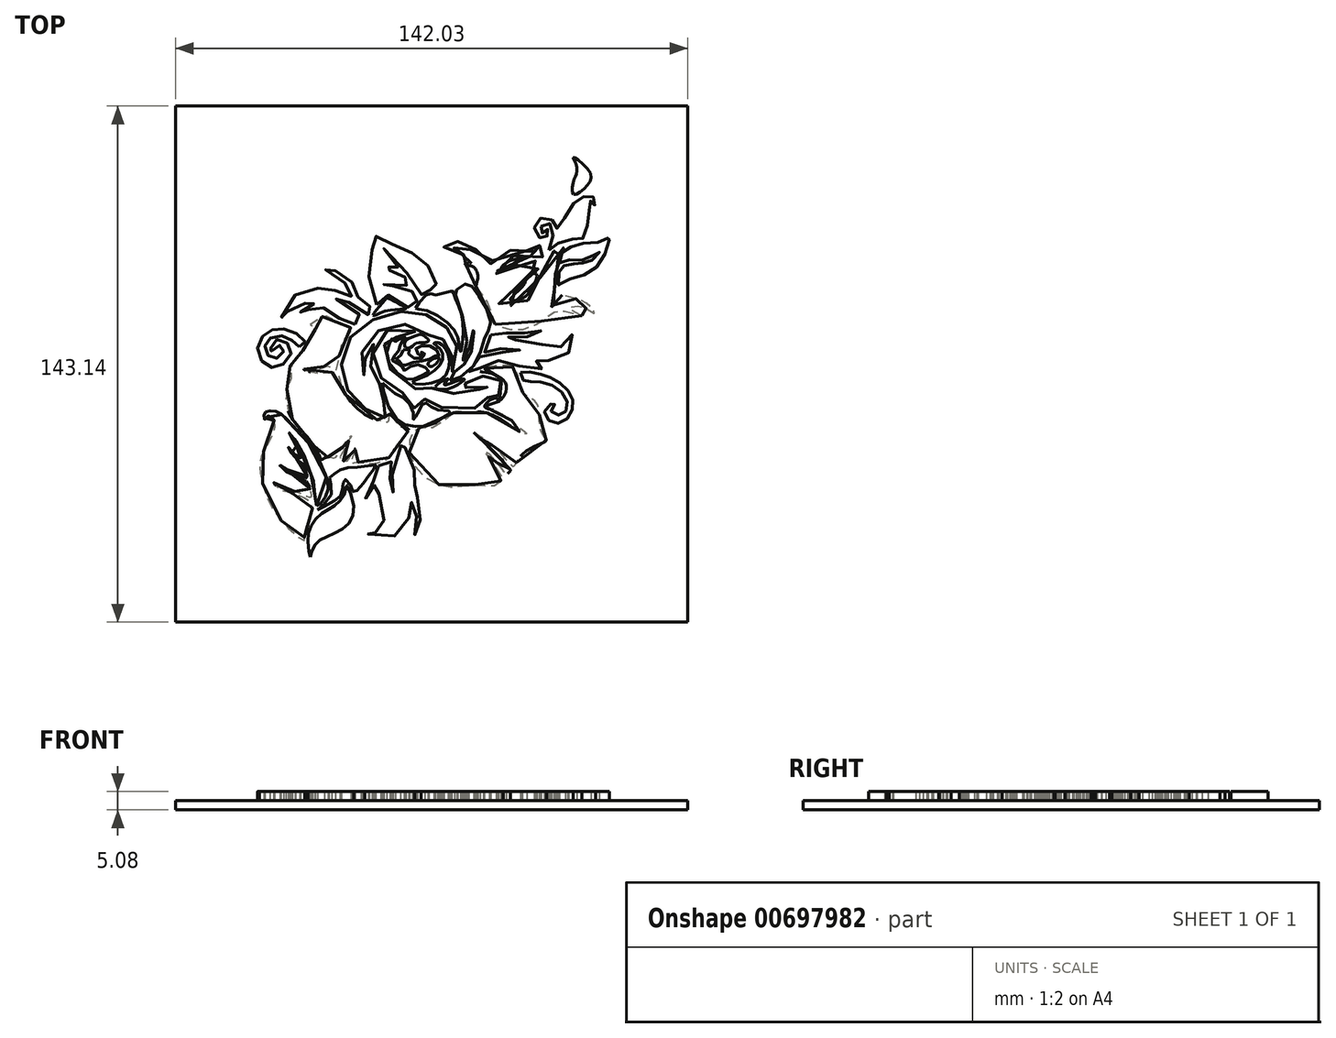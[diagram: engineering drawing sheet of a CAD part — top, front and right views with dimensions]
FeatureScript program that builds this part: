
annotation { "Feature Type Name" : "Feature", "Feature Type Description" : "" }
export const myFeature = defineFeature(function(context is Context, id is Id, definition is map)
    precondition{}
    {
        {
            var Q0;
            Q0=qCreatedBy(makeId("Top.planeOp"),FACE);
            var sketch = newSketch(context, id + "F0", { "sketchPlane" : qUnion([Q0])});
            skLineSegment(sketch, "E0.bottom", {"start": v(-70.24, 72.03) * mm, "end": v(71.8, 72.03) * mm});
            skLineSegment(sketch, "E0.top", {"start": v(-70.24, -71.11) * mm, "end": v(71.8, -71.11) * mm});
            skLineSegment(sketch, "E0.left", {"start": v(-70.24, 72.03) * mm, "end": v(-70.24, -71.11) * mm});
            skLineSegment(sketch, "E0.right", {"start": v(71.8, 72.03) * mm, "end": v(71.8, -71.11) * mm});
            skSolve(sketch);
        }
        {
            var Q0;
            Q0=qCreatedBy(makeId("Top.planeOp"),FACE);
            cPlane(context, id + "F1", {"entities" : qUnion([Q0]), "cplaneType" : CPlaneType.OFFSET, "offset" : 2.54 * mm, "width" : 152.4 * mm, "height" : 152.4 * mm});
        }
        {
            var Q0;
            Q0=makeQuery(id+"F0.imprint","IMPRINT",FACE,{"disambiguationData":[TD([[makeQuery(id+"F0.imprint","IMPRINT",EDGE,{"derivedFrom":sQuery(id+"F0.wireOp",EDGE,"E0.bottom")}),-1.0]])]});
            extrude(context, id + "F2", {"entities" : qUnion([Q0]), "depth" : 2.54 * mm, "offsetDistance" : 25.4 * mm});
        }
        {
            var Q0;
            Q0=makeQuery(id+"F2.opExtrude","CAP_FACE",FACE,{"disambiguationData":[OSD([sQuery(id+"F0.wireOp",EDGE,"E0.bottom"),sQuery(id+"F0.wireOp",EDGE,"E0.top"),sQuery(id+"F0.wireOp",EDGE,"E0.left"),sQuery(id+"F0.wireOp",EDGE,"E0.right")])],"isStart":false});
            var sketch = newSketch(context, id + "F3", { "sketchPlane" : qUnion([Q0])});
            skFitSpline(sketch, "E1", {"points": [v(-35.94, 5.21) * mm, v(-34.32, 6.4) * mm, v(-37.33, 9.33) * mm, v(-42.18, 10.2) * mm, v(-45.56, 8.7) * mm, v(-47.5, 4.27) * mm, v(-44.77, 0) * mm, v(-41.11, 0) * mm, v(-38.06, 3.91) * mm, v(-40.5, 7.1) * mm, v(-43.21, 6.5) * mm, v(-43.93, 3.58) * mm, v(-42.6, 5.3) * mm, v(-40.5, 5.3) * mm, v(-40.68, 3.08) * mm, v(-43.35, 2.02) * mm, v(-45.25, 4.12) * mm, v(-44.95, 6.79) * mm, v(-41.8, 8.33) * mm, v(-38.2, 7.27) * mm, v(-35.94, 5.21) * mm]});
            skSolve(sketch);
        }
        {
            var Q0;
            Q0=makeQuery(id+"F3.imprint","IMPRINT",FACE,{"disambiguationData":[TD([[makeQuery(id+"F3.imprint","IMPRINT",EDGE,{"derivedFrom":sQuery(id+"F3.wireOp",EDGE,"E1")}),1.0]])]});
            extrude(context, id + "F4", {"entities" : qUnion([Q0]), "operationType" : NewBodyOperationType.ADD, "depth" : 2.54 * mm, "offsetDistance" : 25.4 * mm});
        }
        {
            var Q0;
            Q0=qCreatedBy(id+"F1.planeOp",FACE);
            var sketch = newSketch(context, id + "F5", { "sketchPlane" : qUnion([Q0])});
            skFitSpline(sketch, "E2", {"points": [v(-20.47, 11.53) * mm, v(-18.42, 13.18) * mm, v(-25.91, 18.74) * mm, v(-20.95, 17.01) * mm, v(-16.07, 14.1) * mm, v(-16.07, 16.11) * mm, v(-19.16, 18.41) * mm, v(-20.72, 21.86) * mm, v(-24.08, 25.62) * mm, v(-28.9, 26.88) * mm, v(-24.94, 24.5) * mm, v(-21.15, 19.34) * mm, v(-24.94, 20.58) * mm, v(-28.94, 21.4) * mm, v(-37.09, 19.6) * mm, v(-40.97, 12.78) * mm, v(-38.37, 15.97) * mm, v(-33.01, 17.43) * mm, v(-31.62, 17.34) * mm, v(-33.87, 16.32) * mm, v(-35.83, 14.35) * mm, v(-33.16, 15.68) * mm, v(-29.38, 16.15) * mm, v(-24.5, 13.03) * mm, v(-20.47, 11.53) * mm]});
            skSolve(sketch);
        }
        {
            var Q0;
            Q0=makeQuery(id+"F5.imprint","IMPRINT",FACE,{"disambiguationData":[TD([[makeQuery(id+"F5.imprint","IMPRINT",EDGE,{"derivedFrom":sQuery(id+"F5.wireOp",EDGE,"E2")}),1.0]])]});
            extrude(context, id + "F6", {"entities" : qUnion([Q0]), "operationType" : NewBodyOperationType.ADD, "depth" : 2.54 * mm, "offsetDistance" : 25.4 * mm});
        }
        {
            var Q0;
            Q0=qCreatedBy(id+"F1.planeOp",FACE);
            var sketch = newSketch(context, id + "F7", { "sketchPlane" : qUnion([Q0])});
            skFitSpline(sketch, "E3", {"points": [v(-14.47, 17) * mm, v(-12.08, 19.37) * mm, v(-10.76, 19.34) * mm, v(-5.19, 16.12) * mm, v(-4.45, 17.02) * mm, v(-3.25, 18.12) * mm, v(-3.7, 19.39) * mm, v(-4.65, 20.6) * mm, v(-8.74, 22.16) * mm, v(-13.33, 22.03) * mm, v(-10.14, 23) * mm, v(-5.64, 22.3) * mm, v(-6.08, 23.41) * mm, v(-6.89, 24.97) * mm, v(-10.14, 26.28) * mm, v(-12.86, 27.16) * mm, v(-9.57, 27.16) * mm, v(-7.86, 26.51) * mm, v(-12.56, 32.43) * mm, v(-5.4, 24.8) * mm, v(-1.93, 19.73) * mm, v(-1.33, 20.28) * mm, v(0, 21.03) * mm, v(2.38, 20.98) * mm, v(1.83, 23.22) * mm, v(0, 27.49) * mm, v(-3.68, 30.7) * mm, v(-8.37, 33.18) * mm, v(-13.3, 34.82) * mm, v(-14.89, 35.97) * mm, v(-15.46, 33.45) * mm, v(-16.66, 27.43) * mm, v(-14.47, 17) * mm]});
            skSolve(sketch);
        }
        {
            var Q0;
            Q0=makeQuery(id+"F7.imprint","IMPRINT",FACE,{"disambiguationData":[TD([[makeQuery(id+"F7.imprint","IMPRINT",EDGE,{"derivedFrom":sQuery(id+"F7.wireOp",EDGE,"E3")}),1.0]])]});
            extrude(context, id + "F8", {"entities" : qUnion([Q0]), "operationType" : NewBodyOperationType.ADD, "depth" : 2.54 * mm, "offsetDistance" : 25.4 * mm});
        }
        {
            var Q0;
            Q0=makeQuery(id+"F2.opExtrude","CAP_FACE",FACE,{"disambiguationData":[OSD([sQuery(id+"F0.wireOp",EDGE,"E0.bottom"),sQuery(id+"F0.wireOp",EDGE,"E0.top"),sQuery(id+"F0.wireOp",EDGE,"E0.left"),sQuery(id+"F0.wireOp",EDGE,"E0.right")])],"isStart":false});
            var sketch = newSketch(context, id + "F9", { "sketchPlane" : qUnion([Q0])});
            skFitSpline(sketch, "E4", {"points": [v(13.15, 21.94) * mm, v(15.72, 18.44) * mm, v(18.2, 11.98) * mm, v(18.88, 11.18) * mm, v(25.15, 9.95) * mm, v(32.75, 13.51) * mm, v(36.96, 15.31) * mm, v(42.41, 13.88) * mm, v(38.74, 16.03) * mm, v(39.71, 16.4) * mm, v(42.83, 16.35) * mm, v(46.16, 14.51) * mm, v(44.79, 16.6) * mm, v(40.46, 18.72) * mm, v(37.5, 19.43) * mm, v(36.17, 19.7) * mm, v(35.7, 18.87) * mm, v(34.14, 16.35) * mm, v(35.04, 19.33) * mm, v(35.23, 23.76) * mm, v(35.1, 28.34) * mm, v(36.32, 31.34) * mm, v(37.92, 32.7) * mm, v(35.31, 32.12) * mm, v(32.43, 29.72) * mm, v(30.8, 24.09) * mm, v(29.12, 19.93) * mm, v(24.94, 16.98) * mm, v(19.36, 17.1) * mm, v(22.43, 18.85) * mm, v(23.84, 20.87) * mm, v(25.71, 24.06) * mm, v(28.11, 26.11) * mm, v(30.06, 26.68) * mm, v(30.67, 28.18) * mm, v(30, 28.97) * mm, v(27.54, 28.88) * mm, v(23.97, 27.6) * mm, v(21.73, 25.87) * mm, v(18.97, 24.78) * mm, v(18.78, 25.76) * mm, v(20.83, 28.62) * mm, v(24.2, 30.72) * mm, v(29.3, 30.25) * mm, v(32.4, 30.54) * mm, v(32.52, 32.34) * mm, v(31.51, 33.12) * mm, v(30.03, 33.4) * mm, v(30.87, 32.6) * mm, v(30.73, 31.78) * mm, v(28.6, 31.86) * mm, v(26.46, 31.95) * mm, v(21.55, 31.93) * mm, v(18.32, 30.33) * mm, v(17.07, 28.15) * mm, v(16.18, 30.41) * mm, v(13.01, 32.26) * mm, v(10.22, 32.48) * mm, v(8.03, 34.52) * mm, v(8.73, 32.75) * mm, v(6.1, 32.81) * mm, v(3.49, 32.71) * mm, v(7.3, 31.55) * mm, v(10.78, 30.04) * mm, v(12.8, 28.15) * mm, v(11.49, 28.43) * mm, v(10.02, 28.21) * mm, v(11.34, 27.77) * mm, v(12.84, 27) * mm, v(13.58, 24.09) * mm, v(13.15, 21.94) * mm]});
            skSolve(sketch);
        }
        {
            var Q0;
            Q0=makeQuery(id+"F9.imprint","IMPRINT",FACE,{"disambiguationData":[TD([[makeQuery(id+"F9.imprint","IMPRINT",EDGE,{"derivedFrom":sQuery(id+"F9.wireOp",EDGE,"E4")}),1.0]])]});
            extrude(context, id + "F10", {"entities" : qUnion([Q0]), "operationType" : NewBodyOperationType.ADD, "depth" : 2.54 * mm, "offsetDistance" : 25.4 * mm});
        }
        {
            var Q0;
            Q0=qCreatedBy(id+"F1.planeOp",FACE);
            var sketch = newSketch(context, id + "F11", { "sketchPlane" : qUnion([Q0])});
            skFitSpline(sketch, "E5", {"points": [v(25.88, 29.7) * mm, v(21.93, 28.86) * mm, v(20.05, 26.64) * mm, v(22.53, 27.37) * mm, v(23.88, 28.63) * mm, v(25.88, 29.7) * mm]});
            skSolve(sketch);
        }
        {
            var Q0;
            Q0=makeQuery(id+"F11.imprint","IMPRINT",FACE,{"disambiguationData":[TD([[makeQuery(id+"F11.imprint","IMPRINT",EDGE,{"derivedFrom":sQuery(id+"F11.wireOp",EDGE,"E5")}),1.0]])]});
            extrude(context, id + "F12", {"entities" : qUnion([Q0]), "operationType" : NewBodyOperationType.ADD, "depth" : 2.54 * mm, "offsetDistance" : 25.4 * mm});
        }
        {
            var Q0;
            Q0=qCreatedBy(id+"F1.planeOp",FACE);
            var sketch = newSketch(context, id + "F13", { "sketchPlane" : qUnion([Q0])});
            skFitSpline(sketch, "E6", {"points": [v(29.83, 25.45) * mm, v(27.47, 24.85) * mm, v(26.24, 22.34) * mm, v(22.55, 18.26) * mm, v(25.89, 18.76) * mm, v(28.44, 21.31) * mm, v(29.83, 25.45) * mm]});
            skSolve(sketch);
        }
        {
            var Q0;
            Q0=makeQuery(id+"F13.imprint","IMPRINT",FACE,{"disambiguationData":[TD([[makeQuery(id+"F13.imprint","IMPRINT",EDGE,{"derivedFrom":sQuery(id+"F13.wireOp",EDGE,"E6")}),1.0]])]});
            extrude(context, id + "F14", {"entities" : qUnion([Q0]), "operationType" : NewBodyOperationType.ADD, "depth" : 2.54 * mm, "offsetDistance" : 25.4 * mm});
        }
        {
            var Q0;
            Q0=qCreatedBy(id+"F1.planeOp",FACE);
            var sketch = newSketch(context, id + "F15", { "sketchPlane" : qUnion([Q0])});
            skFitSpline(sketch, "E7", {"points": [v(33.28, 32.03) * mm, v(36.18, 34.2) * mm, v(41.06, 35.12) * mm, v(43, 35.65) * mm, v(44.2, 41.55) * mm, v(44.64, 44.66) * mm, v(44.94, 45.8) * mm, v(45.94, 44.52) * mm, v(46.08, 46) * mm, v(44.92, 47.11) * mm, v(42, 46.57) * mm, v(38.63, 42.9) * mm, v(35.62, 38.12) * mm, v(34.77, 39.73) * mm, v(31.8, 41.15) * mm, v(29.4, 39.14) * mm, v(30.28, 35.73) * mm, v(32.24, 35.6) * mm, v(33.04, 36.43) * mm, v(33.01, 37.9) * mm, v(32.38, 36.75) * mm, v(31.07, 37.21) * mm, v(31.04, 38.52) * mm, v(32.65, 39.53) * mm, v(34.64, 38.1) * mm, v(33.28, 32.03) * mm]});
            skSolve(sketch);
        }
        {
            var Q0;
            Q0=makeQuery(id+"F15.imprint","IMPRINT",FACE,{"disambiguationData":[TD([[makeQuery(id+"F15.imprint","IMPRINT",EDGE,{"derivedFrom":sQuery(id+"F15.wireOp",EDGE,"E7")}),1.0]])]});
            extrude(context, id + "F16", {"entities" : qUnion([Q0]), "operationType" : NewBodyOperationType.ADD, "depth" : 2.54 * mm, "offsetDistance" : 25.4 * mm});
        }
        {
            var Q0;
            Q0=qCreatedBy(id+"F1.planeOp",FACE);
            var sketch = newSketch(context, id + "F17", { "sketchPlane" : qUnion([Q0])});
            skFitSpline(sketch, "E8", {"points": [v(40.15, 47.54) * mm, v(43.66, 49.75) * mm, v(44.73, 53.5) * mm, v(40.13, 57.8) * mm, v(40.75, 56.07) * mm, v(40.89, 53.24) * mm, v(40.07, 51.06) * mm, v(40.15, 47.54) * mm]});
            skSolve(sketch);
        }
        {
            var Q0;
            Q0=makeQuery(id+"F17.imprint","IMPRINT",FACE,{"disambiguationData":[TD([[makeQuery(id+"F17.imprint","IMPRINT",EDGE,{"derivedFrom":sQuery(id+"F17.wireOp",EDGE,"E8")}),1.0]])]});
            extrude(context, id + "F18", {"entities" : qUnion([Q0]), "operationType" : NewBodyOperationType.ADD, "depth" : 2.54 * mm, "offsetDistance" : 25.4 * mm});
        }
        {
            var Q0;
            Q0=qCreatedBy(id+"F1.planeOp",FACE);
            var sketch = newSketch(context, id + "F19", { "sketchPlane" : qUnion([Q0])});
            skFitSpline(sketch, "E9", {"points": [v(-15.47, 14) * mm, v(-11.85, 15.19) * mm, v(-6.34, 15.83) * mm, v(-6.92, 16.4) * mm, v(-11.38, 18.72) * mm, v(-12.14, 18.28) * mm, v(-15.47, 14) * mm]});
            skSolve(sketch);
        }
        {
            var Q0;
            Q0=makeQuery(id+"F19.imprint","IMPRINT",FACE,{"disambiguationData":[TD([[makeQuery(id+"F19.imprint","IMPRINT",EDGE,{"derivedFrom":sQuery(id+"F19.wireOp",EDGE,"E9")}),1.0]])]});
            extrude(context, id + "F20", {"entities" : qUnion([Q0]), "operationType" : NewBodyOperationType.ADD, "depth" : 2.54 * mm, "offsetDistance" : 25.4 * mm});
        }
        {
            var Q0;
            Q0=qCreatedBy(id+"F1.planeOp",FACE);
            var sketch = newSketch(context, id + "F21", { "sketchPlane" : qUnion([Q0])});
            skFitSpline(sketch, "E10", {"points": [v(36.07, 25.96) * mm, v(36.12, 21.99) * mm, v(36.65, 22.74) * mm, v(38.91, 23.98) * mm, v(45.13, 26.25) * mm, v(49.24, 31.97) * mm, v(50.03, 35.93) * mm, v(48.92, 34.73) * mm, v(43.4, 34.08) * mm, v(38.54, 32.55) * mm, v(36.44, 30.35) * mm, v(36.23, 27.82) * mm, v(36.7, 28.9) * mm, v(39.94, 29.31) * mm, v(44.63, 29.98) * mm, v(47.32, 31.62) * mm, v(45.68, 29.67) * mm, v(42.9, 28.51) * mm, v(40.3, 28.21) * mm, v(37.42, 27.7) * mm, v(36.07, 25.96) * mm]});
            skSolve(sketch);
        }
        {
            var Q0;
            Q0=makeQuery(id+"F21.imprint","IMPRINT",FACE,{"disambiguationData":[TD([[makeQuery(id+"F21.imprint","IMPRINT",EDGE,{"derivedFrom":sQuery(id+"F21.wireOp",EDGE,"E10")}),1.0]])]});
            extrude(context, id + "F22", {"entities" : qUnion([Q0]), "operationType" : NewBodyOperationType.ADD, "depth" : 2.54 * mm, "offsetDistance" : 25.4 * mm});
        }
        {
            var Q0;
            Q0=qCreatedBy(id+"F1.planeOp",FACE);
            var sketch = newSketch(context, id + "F23", { "sketchPlane" : qUnion([Q0])});
            skFitSpline(sketch, "E11", {"points": [v(17.17, 8.62) * mm, v(15.13, 3.81) * mm, v(16.84, 4.6) * mm, v(20.13, 4.8) * mm, v(25.36, 4.35) * mm, v(24.04, 4.3) * mm, v(20.8, 3.76) * mm, v(14.46, 2.88) * mm, v(12.75, 0) * mm, v(11.08, -1.82) * mm, v(12.97, -1.17) * mm, v(15.43, 0) * mm, v(19.7, 1.43) * mm, v(24.44, 0) * mm, v(28.48, 0) * mm, v(32.61, -1.22) * mm, v(29.46, 1.73) * mm, v(30.3, 1.7) * mm, v(34.96, 1.65) * mm, v(39.18, 4.33) * mm, v(39.78, 8.73) * mm, v(39.35, 7.34) * mm, v(36.37, 5.2) * mm, v(32.49, 5.54) * mm, v(27.45, 6.85) * mm, v(20.84, 7.57) * mm, v(21.94, 7.92) * mm, v(25.88, 8.24) * mm, v(29.02, 8.22) * mm, v(31.15, 9.61) * mm, v(29.02, 9.42) * mm, v(26.07, 9.1) * mm, v(22.75, 9.05) * mm, v(18.76, 9.05) * mm, v(17.17, 8.62) * mm]});
            skSolve(sketch);
        }
        {
            var Q0;
            Q0=makeQuery(id+"F23.imprint","IMPRINT",FACE,{"disambiguationData":[TD([[makeQuery(id+"F23.imprint","IMPRINT",EDGE,{"derivedFrom":sQuery(id+"F23.wireOp",EDGE,"E11")}),1.0]])]});
            extrude(context, id + "F24", {"entities" : qUnion([Q0]), "operationType" : NewBodyOperationType.ADD, "depth" : 2.54 * mm, "offsetDistance" : 25.4 * mm});
        }
        {
            var Q0;
            Q0=qCreatedBy(id+"F1.planeOp",FACE);
            var sketch = newSketch(context, id + "F25", { "sketchPlane" : qUnion([Q0])});
            skFitSpline(sketch, "E12", {"points": [v(25.47, -1.8) * mm, v(26.26, -4.03) * mm, v(28.3, -4.37) * mm, v(32, -4.63) * mm, v(36.46, -6.94) * mm, v(38.43, -10.48) * mm, v(37.32, -13.33) * mm, v(34.83, -13.38) * mm, v(33.8, -11.87) * mm, v(35.09, -10.33) * mm, v(32.57, -11.4) * mm, v(32.64, -14.4) * mm, v(35.35, -15.97) * mm, v(38.63, -14.46) * mm, v(40, -11.06) * mm, v(39.21, -7.68) * mm, v(36.15, -4.65) * mm, v(32.4, -2.73) * mm, v(28.62, -1.82) * mm, v(25.47, -1.8) * mm]});
            skSolve(sketch);
        }
        {
            var Q0;
            Q0=makeQuery(id+"F25.imprint","IMPRINT",FACE,{"disambiguationData":[TD([[makeQuery(id+"F25.imprint","IMPRINT",EDGE,{"derivedFrom":sQuery(id+"F25.wireOp",EDGE,"E12")}),1.0]])]});
            extrude(context, id + "F26", {"entities" : qUnion([Q0]), "operationType" : NewBodyOperationType.ADD, "depth" : 2.54 * mm, "offsetDistance" : 25.4 * mm});
        }
        {
            var Q0;
            Q0=qCreatedBy(id+"F1.planeOp",FACE);
            var sketch = newSketch(context, id + "F27", { "sketchPlane" : qUnion([Q0])});
            skFitSpline(sketch, "E13", {"points": [v(-3.64, 15.96) * mm, v(0, 20.04) * mm, v(1.3, 19.65) * mm, v(6.69, 20.7) * mm, v(6.92, 20.1) * mm, v(8.34, 16.33) * mm, v(9.6, 9.7) * mm, v(8.8, 3.74) * mm, v(8.44, 5.88) * mm, v(6.45, 10.7) * mm, v(-2.04, 15.72) * mm, v(-3.64, 15.96) * mm]});
            skSolve(sketch);
        }
        {
            var Q0;
            Q0=qCreatedBy(id+"F1.planeOp",FACE);
            var sketch = newSketch(context, id + "F28", { "sketchPlane" : qUnion([Q0])});
            skFitSpline(sketch, "E14", {"points": [v(5.88, -4.12) * mm, v(7.69, -1.1) * mm, v(11.35, 2.5) * mm, v(12.45, 10.44) * mm, v(11.21, 4.8) * mm, v(9.13, 1.08) * mm, v(10.55, 7.14) * mm, v(7.15, 21.03) * mm, v(8.03, 21.18) * mm, v(10.7, 22.93) * mm, v(12.56, 21.18) * mm, v(15.5, 16.78) * mm, v(17.15, 10.85) * mm, v(16.25, 9.4) * mm, v(14.7, 4.88) * mm, v(10.88, -1.59) * mm, v(5.88, -4.12) * mm]});
            skSolve(sketch);
        }
        {
            var Q0;
            Q0=makeQuery(id+"F27.imprint","IMPRINT",FACE,{"disambiguationData":[TD([[makeQuery(id+"F27.imprint","IMPRINT",EDGE,{"derivedFrom":sQuery(id+"F27.wireOp",EDGE,"E13")}),-1.0]])]});
            extrude(context, id + "F29", {"entities" : qUnion([Q0]), "operationType" : NewBodyOperationType.ADD, "depth" : 2.54 * mm, "offsetDistance" : 25.4 * mm});
        }
        {
            var Q0;
            Q0=makeQuery(id+"F28.imprint","IMPRINT",FACE,{"disambiguationData":[TD([[makeQuery(id+"F28.imprint","IMPRINT",EDGE,{"derivedFrom":sQuery(id+"F28.wireOp",EDGE,"E14")}),-1.0]])]});
            extrude(context, id + "F30", {"entities" : qUnion([Q0]), "operationType" : NewBodyOperationType.ADD, "depth" : 2.54 * mm, "offsetDistance" : 25.4 * mm});
        }
        {
            var Q0;
            Q0=qCreatedBy(id+"F1.planeOp",FACE);
            var sketch = newSketch(context, id + "F31", { "sketchPlane" : qUnion([Q0])});
            skFitSpline(sketch, "E15", {"points": [v(-12.1, -14.35) * mm, v(-11.75, -11.88) * mm, v(-13.11, -8.32) * mm, v(-13.68, -4.99) * mm, v(-14.9, -2.72) * mm, v(-16.4, 2.64) * mm, v(-15.3, 6.32) * mm, v(-17.2, 3.76) * mm, v(-17.75, -3.13) * mm, v(-18.57, 0) * mm, v(-17.88, 5.28) * mm, v(-11.6, 11.04) * mm, v(-4.3, 10.9) * mm, v(1.08, 8.07) * mm, v(3.3, 7.54) * mm, v(4.35, 6.94) * mm, v(6.23, 3.55) * mm, v(6.32, -2.14) * mm, v(7.41, 2.7) * mm, v(7.34, 7.36) * mm, v(3.5, 11.95) * mm, v(-1.75, 14.52) * mm, v(-8.66, 14.94) * mm, v(-17.07, 11.92) * mm, v(-22.84, 6.19) * mm, v(-24.14, -2.42) * mm, v(-21.31, -8.49) * mm, v(-15.9, -13.13) * mm, v(-12.1, -14.35) * mm]});
            skSolve(sketch);
        }
        {
            var Q0;
            Q0=makeQuery(id+"F31.imprint","IMPRINT",FACE,{"disambiguationData":[TD([[makeQuery(id+"F31.imprint","IMPRINT",EDGE,{"derivedFrom":sQuery(id+"F31.wireOp",EDGE,"E15")}),1.0]])]});
            extrude(context, id + "F32", {"entities" : qUnion([Q0]), "operationType" : NewBodyOperationType.ADD, "depth" : 2.54 * mm, "offsetDistance" : 25.4 * mm});
        }
        {
            var Q0;
            Q0=qCreatedBy(id+"F1.planeOp",FACE);
            var sketch = newSketch(context, id + "F33", { "sketchPlane" : qUnion([Q0])});
            skFitSpline(sketch, "E16", {"points": [v(-4.58, -4.68) * mm, v(1.38, -1.48) * mm, v(3.58, 4.19) * mm, v(1.37, 6.17) * mm, v(2.26, 6.45) * mm, v(5, 4.1) * mm, v(3.73, -3.59) * mm, v(-4.58, -4.68) * mm]});
            skSolve(sketch);
        }
        {
            var Q0;
            Q0=makeQuery(id+"F33.imprint","IMPRINT",FACE,{"disambiguationData":[TD([[makeQuery(id+"F33.imprint","IMPRINT",EDGE,{"derivedFrom":sQuery(id+"F33.wireOp",EDGE,"E16")}),-1.0]])]});
            extrude(context, id + "F34", {"entities" : qUnion([Q0]), "operationType" : NewBodyOperationType.ADD, "depth" : 2.54 * mm, "offsetDistance" : 25.4 * mm});
        }
        {
            var Q0;
            Q0=qCreatedBy(id+"F1.planeOp",FACE);
            var sketch = newSketch(context, id + "F35", { "sketchPlane" : qUnion([Q0])});
            skFitSpline(sketch, "E17", {"points": [v(-6.5, 5.08) * mm, v(-4.94, 5.2) * mm, v(-3.55, 6.2) * mm, v(-1.38, 6.41) * mm, v(0, 7) * mm, v(-1.28, 8.24) * mm, v(-2.4, 8.7) * mm, v(-4.48, 7.99) * mm, v(-6.5, 6.9) * mm, v(-6.5, 5.08) * mm]});
            skSolve(sketch);
        }
        {
            var Q0;
            Q0=qCreatedBy(id+"F1.planeOp",FACE);
            var sketch = newSketch(context, id + "F36", { "sketchPlane" : qUnion([Q0])});
            skFitSpline(sketch, "E18", {"points": [v(1.28, 0) * mm, v(2.86, 2.23) * mm, v(0, 1.03) * mm, v(0, 0) * mm, v(1.28, 0) * mm]});
            skSolve(sketch);
        }
        {
            var Q0;
            Q0 = qSketchRegion(id + "F36", true);
            extrude(context, id + "F37", {"entities" : qUnion([Q0]), "operationType" : NewBodyOperationType.ADD, "depth" : 2.54 * mm, "offsetDistance" : 25.4 * mm});
        }
        {
            var Q0;
            Q0=qCreatedBy(id+"F1.planeOp",FACE);
            var sketch = newSketch(context, id + "F38", { "sketchPlane" : qUnion([Q0])});
            skFitSpline(sketch, "E19", {"points": [v(-7.07, 4.37) * mm, v(-5.4, 4.41) * mm, v(-5.56, 3.37) * mm, v(-3.48, 1.91) * mm, v(-1.25, 2.65) * mm, v(-1.5, 3.78) * mm, v(-2.13, 3.72) * mm, v(-2.01, 2.57) * mm, v(-2.98, 3.25) * mm, v(-3.53, 4.86) * mm, v(-1.18, 5.61) * mm, v(2.14, 4.53) * mm, v(2.83, 2.8) * mm, v(1.94, 2.72) * mm, v(0, 1.75) * mm, v(-3.53, 1.14) * mm, v(-6.79, 0) * mm, v(-7.22, 0) * mm, v(-7.88, 1.08) * mm, v(-9.23, 1.71) * mm, v(-7.81, 2.88) * mm, v(-7.07, 4.37) * mm]});
            skSolve(sketch);
        }
        {
            var Q0;
            Q0=makeQuery(id+"F38.imprint","IMPRINT",FACE,{"disambiguationData":[TD([[makeQuery(id+"F38.imprint","IMPRINT",EDGE,{"derivedFrom":sQuery(id+"F38.wireOp",EDGE,"E19")}),-1.0]])]});
            extrude(context, id + "F39", {"entities" : qUnion([Q0]), "operationType" : NewBodyOperationType.ADD, "depth" : 2.54 * mm, "offsetDistance" : 25.4 * mm});
        }
        {
            var Q0;
            Q0=makeQuery(id+"F35.imprint","IMPRINT",FACE,{"disambiguationData":[TD([[makeQuery(id+"F35.imprint","IMPRINT",EDGE,{"derivedFrom":sQuery(id+"F35.wireOp",EDGE,"E17")}),1.0]])]});
            extrude(context, id + "F40", {"entities" : qUnion([Q0]), "operationType" : NewBodyOperationType.ADD, "depth" : 2.54 * mm, "offsetDistance" : 25.4 * mm});
        }
        {
            var Q0;
            Q0=qCreatedBy(id+"F1.planeOp",FACE);
            var sketch = newSketch(context, id + "F41", { "sketchPlane" : qUnion([Q0])});
            skFitSpline(sketch, "E20", {"points": [v(-3.6, 9.6) * mm, v(-10.12, 10.27) * mm, v(-14.65, 6.2) * mm, v(-15.3, 0) * mm, v(-11.84, -4.62) * mm, v(-7.26, -7.5) * mm, v(-5.09, -9.62) * mm, v(-3.88, -11.87) * mm, v(-3.36, -11.26) * mm, v(-1.29, -9.26) * mm, v(0, -9.61) * mm, v(2.76, -11.29) * mm, v(12.07, -11.92) * mm, v(14.88, -10.66) * mm, v(15.86, -9.33) * mm, v(18.65, -7.04) * mm, v(19.1, -8.27) * mm, v(20.14, -7.04) * mm, v(20.6, -4.83) * mm, v(18.47, -3.29) * mm, v(15.8, -2.81) * mm, v(11.76, -3.77) * mm, v(9.97, -5) * mm, v(7.8, -6.31) * mm, v(11.92, -5.75) * mm, v(14.93, -5.57) * mm, v(16.81, -6.22) * mm, v(15.79, -6.25) * mm, v(13.76, -6.58) * mm, v(8.45, -7.4) * mm, v(3.1, -7.66) * mm, v(0, -5.9) * mm, v(-1.23, -6.4) * mm, v(-4.69, -6.1) * mm, v(-11.46, 0) * mm, v(-12.61, 5.04) * mm, v(-9.91, 8.46) * mm, v(-9.13, 7.9) * mm, v(-7.1, 8.97) * mm, v(-3.6, 9.6) * mm]});
            skSolve(sketch);
        }
        {
            var Q0;
            Q0=makeQuery(id+"F41.imprint","IMPRINT",FACE,{"disambiguationData":[TD([[makeQuery(id+"F41.imprint","IMPRINT",EDGE,{"derivedFrom":sQuery(id+"F41.wireOp",EDGE,"E20")}),1.0]])]});
            extrude(context, id + "F42", {"entities" : qUnion([Q0]), "operationType" : NewBodyOperationType.ADD, "depth" : 2.54 * mm, "offsetDistance" : 25.4 * mm});
        }
        {
            var Q0;
            Q0=qCreatedBy(id+"F1.planeOp",FACE);
            var sketch = newSketch(context, id + "F43", { "sketchPlane" : qUnion([Q0])});
            skFitSpline(sketch, "E21", {"points": [v(-6.1, -3.76) * mm, v(-2.94, -3.08) * mm, v(0, -1.49) * mm, v(-1.9, 0) * mm, v(-4.67, 0) * mm, v(-6.95, -1.3) * mm, v(-7.58, 0) * mm, v(-9.7, 1.07) * mm, v(-10.1, 2.01) * mm, v(-8.62, 3.77) * mm, v(-8.09, 5.12) * mm, v(-7.2, 7.13) * mm, v(-6.45, 7.87) * mm, v(-8.03, 7.53) * mm, v(-9.17, 6.7) * mm, v(-10.2, 7.43) * mm, v(-10.81, 6.48) * mm, v(-11.48, 2.09) * mm, v(-6.1, -3.76) * mm]});
            skSolve(sketch);
        }
        {
            var Q0;
            Q0=makeQuery(id+"F43.imprint","IMPRINT",FACE,{"disambiguationData":[TD([[makeQuery(id+"F43.imprint","IMPRINT",EDGE,{"derivedFrom":sQuery(id+"F43.wireOp",EDGE,"E21")}),1.0]])]});
            extrude(context, id + "F44", {"entities" : qUnion([Q0]), "operationType" : NewBodyOperationType.ADD, "depth" : 2.54 * mm, "offsetDistance" : 25.4 * mm});
        }
        {
            var Q0;
            Q0=qCreatedBy(id+"F1.planeOp",FACE);
            var sketch = newSketch(context, id + "F45", { "sketchPlane" : qUnion([Q0])});
            skFitSpline(sketch, "E22", {"points": [v(-12.8, -4.77) * mm, v(-10.54, -6.92) * mm, v(-6.69, -9.1) * mm, v(-4.3, -12.9) * mm, v(-4.2, -15) * mm, v(-3.65, -14.15) * mm, v(-2.26, -11.56) * mm, v(-1.36, -10.24) * mm, v(0, -10.8) * mm, v(2.2, -12.14) * mm, v(6.27, -12.78) * mm, v(4.8, -13.83) * mm, v(0.9, -16.26) * mm, v(-5.04, -16.73) * mm, v(-10.23, -13.08) * mm, v(-12.8, -4.77) * mm]});
            skSolve(sketch);
        }
        {
            var Q0;
            Q0=makeQuery(id+"F45.imprint","IMPRINT",FACE,{"disambiguationData":[TD([[makeQuery(id+"F45.imprint","IMPRINT",EDGE,{"derivedFrom":sQuery(id+"F45.wireOp",EDGE,"E22")}),-1.0]])]});
            extrude(context, id + "F46", {"entities" : qUnion([Q0]), "operationType" : NewBodyOperationType.ADD, "depth" : 2.54 * mm, "offsetDistance" : 25.4 * mm});
        }
        {
            var Q0;
            Q0=qCreatedBy(id+"F1.planeOp",FACE);
            var sketch = newSketch(context, id + "F47", { "sketchPlane" : qUnion([Q0])});
            skFitSpline(sketch, "E23", {"points": [v(1.81, -5.79) * mm, v(5.48, -6.34) * mm, v(9.83, -3.77) * mm, v(8.62, -3.91) * mm, v(4.25, -5.22) * mm, v(5.34, -3.6) * mm, v(1.81, -5.79) * mm]});
            skSolve(sketch);
        }
        {
            var Q0;
            Q0 = qSketchRegion(id + "F47", true);
            extrude(context, id + "F48", {"entities" : qUnion([Q0]), "operationType" : NewBodyOperationType.ADD, "depth" : 2.54 * mm, "offsetDistance" : 25.4 * mm});
        }
        {
            var Q0;
            Q0=qCreatedBy(id+"F1.planeOp",FACE);
            var sketch = newSketch(context, id + "F49", { "sketchPlane" : qUnion([Q0])});
            skFitSpline(sketch, "E24", {"points": [v(-34.67, -0.96) * mm, v(-32.33, -1.34) * mm, v(-31.25, -1.34) * mm, v(-28.06, 0) * mm, v(-25.44, -1.11) * mm, v(-24.23, 5.82) * mm, v(-21.2, 10.24) * mm, v(-23.02, 11.03) * mm, v(-28.74, 13.84) * mm, v(-30.55, 12.91) * mm, v(-32.93, 11.12) * mm, v(-31.44, 10.16) * mm, v(-32.86, 8.43) * mm, v(-33.86, 5.34) * mm, v(-37.02, 2.45) * mm, v(-37.02, 1.14) * mm, v(-38.5, 0) * mm, v(-37.91, -1.61) * mm, v(-38.91, -5.28) * mm, v(-39.57, -9.06) * mm, v(-38.4, -13.91) * mm, v(-34.08, -19.31) * mm, v(-31.2, -23.3) * mm, v(-29.53, -26.02) * mm, v(-28.9, -25.56) * mm, v(-27.31, -25.32) * mm, v(-26.06, -25.54) * mm, v(-24.7, -23.7) * mm, v(-22.9, -21.05) * mm, v(-21.49, -19.32) * mm, v(-22, -20.3) * mm, v(-23.57, -23.4) * mm, v(-24.52, -25.75) * mm, v(-22.98, -26.54) * mm, v(-21.57, -24.53) * mm, v(-20.5, -22.98) * mm, v(-20.83, -24.58) * mm, v(-21.5, -26.93) * mm, v(-20.13, -26.8) * mm, v(-16.14, -27.06) * mm, v(-10.96, -25.42) * mm, v(-8.77, -21.85) * mm, v(-5.6, -17.65) * mm, v(-7.9, -16.53) * mm, v(-10.94, -13.35) * mm, v(-11.26, -15.52) * mm, v(-12.57, -15.48) * mm, v(-16.51, -14.2) * mm, v(-23.34, -7.5) * mm, v(-24.85, -3.11) * mm, v(-26.46, -1.92) * mm, v(-31.25, -2.01) * mm, v(-34.67, -0.96) * mm]});
            skSolve(sketch);
        }
        {
            var Q0;
            Q0=makeQuery(id+"F49.imprint","IMPRINT",FACE,{"disambiguationData":[TD([[makeQuery(id+"F49.imprint","IMPRINT",EDGE,{"derivedFrom":sQuery(id+"F49.wireOp",EDGE,"E24")}),1.0]])]});
            extrude(context, id + "F50", {"entities" : qUnion([Q0]), "operationType" : NewBodyOperationType.ADD, "depth" : 2.54 * mm, "offsetDistance" : 25.4 * mm});
        }
        {
            var Q0;
            Q0=qCreatedBy(id+"F1.planeOp",FACE);
            var sketch = newSketch(context, id + "F51", { "sketchPlane" : qUnion([Q0])});
            skFitSpline(sketch, "E25", {"points": [v(6.86, -12.95) * mm, v(2.16, -16.88) * mm, v(-3.66, -17.5) * mm, v(-4.67, -19.08) * mm, v(-5.55, -22.48) * mm, v(-2.6, -29.6) * mm, v(4.04, -33.33) * mm, v(9.2, -33.38) * mm, v(14.28, -33.03) * mm, v(17.96, -33.32) * mm, v(18.9, -32.64) * mm, v(20.57, -31.43) * mm, v(20.07, -30.54) * mm, v(17.23, -26) * mm, v(15.3, -23.57) * mm, v(16.59, -24.31) * mm, v(19.36, -27.43) * mm, v(21.6, -30.12) * mm, v(22.15, -29.53) * mm, v(22.7, -28.93) * mm, v(22.03, -28.28) * mm, v(19.43, -25.2) * mm, v(12.43, -18.46) * mm, v(13.96, -19.36) * mm, v(18.95, -23.29) * mm, v(23.39, -27.82) * mm, v(24, -27.33) * mm, v(27.26, -23.47) * mm, v(32.58, -20.66) * mm, v(32.02, -19.66) * mm, v(30.81, -16.98) * mm, v(30.56, -12.6) * mm, v(29.76, -10.13) * mm, v(26.45, -7.88) * mm, v(25.26, -5.49) * mm, v(24.53, -2.1) * mm, v(22.7, 0) * mm, v(20.94, 0) * mm, v(16.49, -0.3) * mm, v(14.25, -1.55) * mm, v(17.2, -2.1) * mm, v(20.84, -4.15) * mm, v(21.5, -5.83) * mm, v(20.54, -8.84) * mm, v(19.1, -9.94) * mm, v(19.12, -9.2) * mm, v(17.74, -9.09) * mm, v(15.43, -11.25) * mm, v(16.72, -11.98) * mm, v(21.34, -13.94) * mm, v(24.97, -17.02) * mm, v(27.17, -18.86) * mm, v(25.26, -18.32) * mm, v(21.54, -15.87) * mm, v(15.33, -12.9) * mm, v(10.52, -12.96) * mm, v(6.86, -12.95) * mm]});
            skSolve(sketch);
        }
        {
            var Q0;
            Q0=makeQuery(id+"F51.imprint","IMPRINT",FACE,{"disambiguationData":[TD([[makeQuery(id+"F51.imprint","IMPRINT",EDGE,{"derivedFrom":sQuery(id+"F51.wireOp",EDGE,"E25")}),1.0]])]});
            extrude(context, id + "F52", {"entities" : qUnion([Q0]), "operationType" : NewBodyOperationType.ADD, "depth" : 2.54 * mm, "offsetDistance" : 25.4 * mm});
        }
        {
            var Q0;
            Q0=qCreatedBy(id+"F1.planeOp",FACE);
            var sketch = newSketch(context, id + "F53", { "sketchPlane" : qUnion([Q0])});
            skFitSpline(sketch, "E26", {"points": [v(-30.78, -39.9) * mm, v(-27.01, -35.61) * mm, v(-27.63, -31.26) * mm, v(-26.34, -30.1) * mm, v(-23.61, -28.4) * mm, v(-18.58, -28.04) * mm, v(-14.75, -27.51) * mm, v(-15.59, -29.03) * mm, v(-18.14, -32.6) * mm, v(-20.78, -35.1) * mm, v(-21.42, -33.72) * mm, v(-23.3, -31.5) * mm, v(-23.74, -32.97) * mm, v(-24.22, -35.58) * mm, v(-26.27, -37.52) * mm, v(-30.78, -39.9) * mm]});
            skSolve(sketch);
        }
        {
            var Q0;
            Q0=makeQuery(id+"F53.imprint","IMPRINT",FACE,{"disambiguationData":[TD([[makeQuery(id+"F53.imprint","IMPRINT",EDGE,{"derivedFrom":sQuery(id+"F53.wireOp",EDGE,"E26")}),-1.0]])]});
            extrude(context, id + "F54", {"entities" : qUnion([Q0]), "operationType" : NewBodyOperationType.ADD, "depth" : 2.54 * mm, "offsetDistance" : 25.4 * mm});
        }
        {
            var Q0;
            Q0=qCreatedBy(id+"F1.planeOp",FACE);
            var sketch = newSketch(context, id + "F55", { "sketchPlane" : qUnion([Q0])});
            skFitSpline(sketch, "E27", {"points": [v(-32.82, -53) * mm, v(-32.28, -50.94) * mm, v(-30.17, -48.38) * mm, v(-26.45, -46.62) * mm, v(-22.47, -43.98) * mm, v(-20.79, -38.87) * mm, v(-22.8, -33.1) * mm, v(-23.01, -34.5) * mm, v(-24.6, -37.44) * mm, v(-27.16, -39.48) * mm, v(-30.48, -41.64) * mm, v(-32.97, -45.14) * mm, v(-33.52, -49.2) * mm, v(-32.82, -53) * mm]});
            skSolve(sketch);
        }
        {
            var Q0;
            Q0=makeQuery(id+"F55.imprint","IMPRINT",FACE,{"disambiguationData":[TD([[makeQuery(id+"F55.imprint","IMPRINT",EDGE,{"derivedFrom":sQuery(id+"F55.wireOp",EDGE,"E27")}),1.0]])]});
            extrude(context, id + "F56", {"entities" : qUnion([Q0]), "operationType" : NewBodyOperationType.ADD, "depth" : 2.54 * mm, "offsetDistance" : 25.4 * mm});
        }
        {
            var Q0;
            Q0=qCreatedBy(id+"F1.planeOp",FACE);
            var sketch = newSketch(context, id + "F57", { "sketchPlane" : qUnion([Q0])});
            skFitSpline(sketch, "E28", {"points": [v(-13.9, -27.74) * mm, v(-10.54, -26.04) * mm, v(-10.6, -27.9) * mm, v(-10.76, -31.48) * mm, v(-10.04, -35.38) * mm, v(-9.86, -32.97) * mm, v(-9.86, -28.24) * mm, v(-6.7, -20.35) * mm, v(-6.35, -24.35) * mm, v(-3.5, -29.92) * mm, v(-3.7, -32.34) * mm, v(-4, -34.78) * mm, v(-3.17, -36.54) * mm, v(-2.27, -42.22) * mm, v(-3.8, -47.2) * mm, v(-3.6, -44.27) * mm, v(-3.66, -40.34) * mm, v(-4.69, -37.84) * mm, v(-5.09, -39.91) * mm, v(-6.29, -43.69) * mm, v(-11.73, -47.94) * mm, v(-17.76, -46.12) * mm, v(-15.07, -46.36) * mm, v(-12.5, -44.53) * mm, v(-13.3, -38.7) * mm, v(-14.5, -32.3) * mm, v(-15.68, -33.9) * mm, v(-17.45, -36.84) * mm, v(-17.17, -34.8) * mm, v(-14.38, -30.16) * mm, v(-13.9, -27.74) * mm]});
            skSolve(sketch);
        }
        {
            var Q0;
            Q0=makeQuery(id+"F57.imprint","IMPRINT",FACE,{"disambiguationData":[TD([[makeQuery(id+"F57.imprint","IMPRINT",EDGE,{"derivedFrom":sQuery(id+"F57.wireOp",EDGE,"E28")}),-1.0]])]});
            extrude(context, id + "F58", {"entities" : qUnion([Q0]), "operationType" : NewBodyOperationType.ADD, "depth" : 2.54 * mm, "offsetDistance" : 25.4 * mm});
        }
        {
            var Q0;
            Q0=qCreatedBy(id+"F1.planeOp",FACE);
            var sketch = newSketch(context, id + "F59", { "sketchPlane" : qUnion([Q0])});
            skFitSpline(sketch, "E29", {"points": [v(-31.08, -38.84) * mm, v(-28.2, -35.2) * mm, v(-28.96, -29.62) * mm, v(-32.23, -22.96) * mm, v(-37.66, -16.58) * mm, v(-41.76, -12.9) * mm, v(-44.72, -12.6) * mm, v(-45.65, -13.62) * mm, v(-45.42, -15) * mm, v(-44.87, -14.08) * mm, v(-43.98, -13.98) * mm, v(-42.89, -15.15) * mm, v(-43.43, -19.23) * mm, v(-46.5, -25.27) * mm, v(-46.78, -29.3) * mm, v(-44.53, -37.13) * mm, v(-39.7, -44.2) * mm, v(-34.53, -48.53) * mm, v(-34.5, -46.55) * mm, v(-32.7, -41.75) * mm, v(-32.57, -38.16) * mm, v(-35.26, -36.35) * mm, v(-38.57, -35.22) * mm, v(-41.3, -34.34) * mm, v(-42.97, -32.4) * mm, v(-41.51, -33.47) * mm, v(-38.88, -34.51) * mm, v(-36.38, -35.06) * mm, v(-32.63, -36.34) * mm, v(-32.9, -34.3) * mm, v(-33.24, -32.94) * mm, v(-35.4, -31.13) * mm, v(-39.21, -29.6) * mm, v(-41.3, -27.63) * mm, v(-40.05, -28.37) * mm, v(-37.36, -29.65) * mm, v(-33.7, -31.1) * mm, v(-34.02, -29.86) * mm, v(-34.65, -27.39) * mm, v(-35.77, -26.62) * mm, v(-37.69, -24.74) * mm, v(-39.03, -22.58) * mm, v(-37.97, -23.63) * mm, v(-35.58, -25.78) * mm, v(-36.15, -23.56) * mm, v(-37.52, -20.75) * mm, v(-38.74, -18.57) * mm, v(-35.97, -22.2) * mm, v(-32.97, -29.33) * mm, v(-31.66, -33.99) * mm, v(-31.08, -38.84) * mm]});
            skSolve(sketch);
        }
        {
            var Q0;
            Q0=makeQuery(id+"F59.imprint","IMPRINT",FACE,{"disambiguationData":[TD([[makeQuery(id+"F59.imprint","IMPRINT",EDGE,{"derivedFrom":sQuery(id+"F59.wireOp",EDGE,"E29")}),1.0]])]});
            extrude(context, id + "F60", {"entities" : qUnion([Q0]), "operationType" : NewBodyOperationType.ADD, "depth" : 2.54 * mm, "offsetDistance" : 25.4 * mm});
        }
    });
